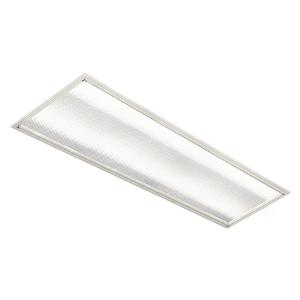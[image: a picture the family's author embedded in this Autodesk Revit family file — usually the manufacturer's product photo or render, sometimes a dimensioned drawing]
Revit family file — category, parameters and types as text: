
# Revit family: 3f_filippi_-_l_320_sp_3f_filippi_-_21287_-_l_322x18w_led_sp_296x1196
name_source: partatom
category: Lighting Fixtures
units: mm (PartAtom-declared; Revit-internal decimal feet)

## family parameters
Cut with Voids When Loaded = No
Host = Face
Light Source = No
Part Type = Normal
Room Calculation Point = No
Round Connector Dimension = Use Diameter
Shared = No

## types (1)
- 3F Filippi - L 320 SP (1 x LED, 5114 lm, 40 W, 4000 K)
    Apparent Load = 40 VA
    Approval mark = ENEC
    CIE Flux Codes = 61 91 99 100 100
    Color Rendering = 80
    Color Temperature = 4000 K
    Control Gear = Electronic ballast
    Default Elevation = 1800 mm
    Description = ILLUMINOTECHNICAL
Luminous efficiency 100% (DLOR 100%, ULOR 0%).
Initial luminous flux of the luminaire 5114 lm.
Direct symmetric distribution.
Installation Interdistance Transv.D = 1.17 x hu - Long.D = 1.20 x hu.
Average luminance <3000 cd/m² for radial angles >65°.
Tabular UGR (CIE 117 - 4H-8H; S=0.25H; 70/50/20): RUG 18.4 - 19.1.
Beam angle: 91° - 95°.
Luminous efficacy 128 lm/W.
Lifetime (L93/B10): 30000 h. (tq+25°C)
Lifetime (L90/B10): 50000 h. (tq+25°C)
Lifetime (L85/B10): 80000 h. (tq+25°C)
Lifetime (L80/B10): 100000 h. (tq+25°C)
Sudden decreased luminous flux after 50000 hours: 0% (C0).
Photobiological safety in compliance with IEC/TR 62778: RG0 risk exempt, (IEC 62471).
In compliance with IEC/EN 62722-2-1 - IEC/EN 62717 standards.

SOURCE
2 linear LED modules 18W/840.
Energy efficiency class (UE 2019/2020 - UE 2019/2015): D.
CIE 13.3 Colour rendering index: CRI >80 (R9 <50%).
IES TM-30 Fidelity Index: Rf = 84 Rg = 95.
CCT nominal colour temperature 4000 K.
Colour initial tolerance (MacAdam): SDCM 2.

MECHANICAL
Steel body, painted in white polyester.
Transparent methacrylate (PMMA) flat diffuser, multilenticular exterior, anti-glare, locked to the white painted aluminium perimeter frame with sealing gasket, hinged opening.
Luminaire with limited surface temperature. - D - (EN 60598-2-24)
Dimensions: 1196x296 mm, height 95 mm. Weight 4.715 kg.
IP54 protection degree for exposed part, IP20 for recessed part.
Mechanical strength to impacts IK06 (1 joule).
Glow-wire test resistance 650°C.

ELECTRICAL
Halogen Free electronic wiring 230V-50/60Hz, power factor 0.95, THD <25%, constant output current, SELV, class I, 1 driver.
Power of the luminaire 40 W.
CE - IEC 60598-1 - EN 60598-1.
SAFE FLICKER: PstLM=<1 and SVM=<0.4 (IEC TR 61547-1 and IEC TR 63158), to ensure a more comfortable and safe light.
Luminaire compliant with EN 60598-2-22 for power supply from a centralised emergency system CPSS (Central Power Supply System), not incorporated in the luminaire - high risk areas excluded. The default power and flux are 100% in AC and 100% in DC.
Ambient temperature from 0°C to +25°C.
Temperature class T6 max 85°C.
Relative humidity UR: <85%.

INSTALLATION
Lay-in recessed fitting / Pull-up recessed fitting with brackets.
False ceiling carving: 280x1180 mm.
All accessories dedicated to this product are available on the Catalog and on our website www.3F-Filippi.com.

APPLICATIONS
Suitable product for food production plants (HACCP), IFS (Food Version 6), BRC (GSFS Food Version 7).
Environments: sterilized, aseptic.
In environments with VDU's, managerial offices and staterooms, environments involving accurate visual tasks where a diffused and soft light for an optimum visual comfort and the source total shielding are required.

WARNING
Luminaire designed for disposal/recycling at end-of-life.
Replaceable (LED only) light source by a professional. Replaceable control gear by a professional.
    Height = 0 mm  [stored 0 ft]
    Lamp = 1 x LED
    Lamp Light Flux = 5114 lm
    Lamp Power = 40 W
    Lamp count = 1
    Length = 1196 mm
    Lifetime = 50000 h
    Luminous efficacy = 128 lm/W
    Manufacturer = 3F Filippi
    ModVariant = No
    Model = 3F Filippi - 21287 - L 322x18W LED SP 296x1196
    Mounting Place = Ceiling
    Mounting Type = Recessed
    Number of Poles = 1
    OnlyDefault = Yes
    Power Factor = 1
    Product Name = 3F Filippi - L 320 SP
    Product group = recessed luminaire
    ProductGroupID = 4
    Protection Class = Protection class I
    Protection Degree = IP 20
    RLX_Detail_Level = 1
    RLX_Emergency_Light_Flux = 0 lm
    RLX_Emergency_Type = 0
    RLX_Emergency_Type_DB = No
    RlxData = <blob elided: 35945 chars, md5=c2259a5c>
    Socket = socket
    Standby Power = 0 W
    System Light Flux = 5114 lm
    System Power = 40 W
    Type Comments = Product without accessories
    Type Image = 3ffilippi_l_320_led_sp_1196.jpg
    URL = http://relux.com
    VarID = ---
    Voltage = 0 V
    Weight = 0.00 kg
    Width = 296 mm

note: [stored X ft] marks values corroborated as IEEE doubles in the binary element streams (Revit-internal decimal feet)

## geometry (parser evidence)
native form markers: Blend x4, Sweep x9
no freeform markers — native parametric forms only
